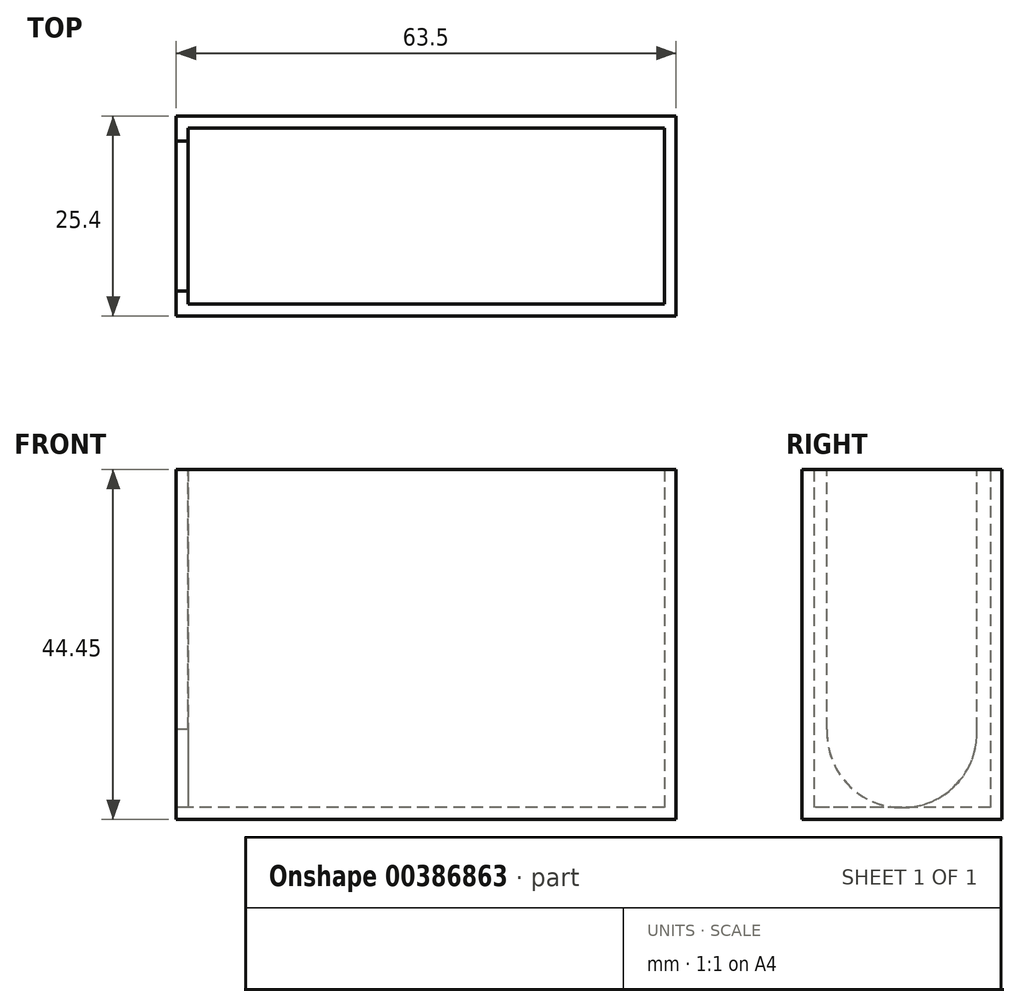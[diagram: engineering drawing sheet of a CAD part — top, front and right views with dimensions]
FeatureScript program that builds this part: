
annotation { "Feature Type Name" : "Feature", "Feature Type Description" : "" }
export const myFeature = defineFeature(function(context is Context, id is Id, definition is map)
    precondition{}
    {
        {
            var Q0;
            Q0=qCreatedBy(makeId("Top.planeOp"),FACE);
            var sketch = newSketch(context, id + "F0", { "sketchPlane" : qUnion([Q0])});
            skLineSegment(sketch, "E0.bottom", {"start": v(31.75, 12.7) * mm, "end": v(-31.75, 12.7) * mm});
            skLineSegment(sketch, "E0.top", {"start": v(31.75, -12.7) * mm, "end": v(-31.75, -12.7) * mm});
            skLineSegment(sketch, "E0.left", {"start": v(31.75, 12.7) * mm, "end": v(31.75, -12.7) * mm});
            skLineSegment(sketch, "E0.right", {"start": v(-31.75, 12.7) * mm, "end": v(-31.75, -12.7) * mm});
            skPoint(sketch, "E0.middle", {"position": v(0, 0) * mm});
            skSolve(sketch);
        }
        {
            var Q0;
            Q0=makeQuery(id+"F0.imprint","IMPRINT",FACE,{"disambiguationData":[TD([[makeQuery(id+"F0.imprint","IMPRINT",EDGE,{"derivedFrom":sQuery(id+"F0.wireOp",EDGE,"E0.bottom")}),1.0]])]});
            extrude(context, id + "F1", {"entities" : qUnion([Q0]), "depth" : 44.45 * mm});
        }
        {
            var Q0;
            Q0=makeQuery(id+"F1.opExtrude","CAP_FACE",FACE,{"disambiguationData":[OSD([sQuery(id+"F0.wireOp",EDGE,"E0.bottom"),sQuery(id+"F0.wireOp",EDGE,"E0.top"),sQuery(id+"F0.wireOp",EDGE,"E0.left"),sQuery(id+"F0.wireOp",EDGE,"E0.right")])],"isStart":false});
            shell(context, id + "F2", {"entities" : qUnion([Q0]), "thickness" : 1.5 * mm});
        }
        {
            var Q0;
            Q0=makeQuery(id+"F1.opExtrude","SWEPT_FACE",FACE,{"disambiguationData":[OSD([sQuery(id+"F0.wireOp",EDGE,"E0.right")])]});
            var sketch = newSketch(context, id + "F3", { "sketchPlane" : qUnion([Q0])});
            skCircle(sketch, "E1", {"center": v(0, 11.03) * mm, "radius": 9.53 * mm});
            skLineSegment(sketch, "E2.bottom", {"start": v(9.52, 11.43) * mm, "end": v(-9.53, 11.43) * mm});
            skLineSegment(sketch, "E2.top", {"start": v(9.52, 44.45) * mm, "end": v(-9.53, 44.45) * mm});
            skLineSegment(sketch, "E2.left", {"start": v(9.52, 11.43) * mm, "end": v(9.52, 44.45) * mm});
            skLineSegment(sketch, "E2.right", {"start": v(-9.53, 11.43) * mm, "end": v(-9.53, 44.45) * mm});
            skSolve(sketch);
        }
        {
            var Q0;
            {var subQ0=sQuery(id+"F3.wireOp",EDGE,"E2.bottom");var subQ1=sQuery(id+"F3.wireOp",EDGE,"E1");var subQ3=makeQuery(id+"F3.imprint","INTERSECT",VERTEX,{"derivedFrom":[subQ1,subQ0]});Q0=makeQuery(id+"F3.imprint","IMPRINT",FACE,{"disambiguationData":[TD([[makeQuery(id+"F3.imprint","IMPRINT",EDGE,{"disambiguationData":[TD([[subQ3,-1.0]])],"derivedFrom":subQ1}),1.0]])]});}
            var Q1;
            {var subQ0=sQuery(id+"F3.wireOp",EDGE,"E2.bottom");var subQ1=sQuery(id+"F3.wireOp",EDGE,"E1");var subQ2=makeQuery(id+"F3.imprint","INTERSECT",VERTEX,{"derivedFrom":[subQ1,subQ0]});Q1=makeQuery(id+"F3.imprint","IMPRINT",FACE,{"disambiguationData":[TD([[makeQuery(id+"F3.imprint","IMPRINT",EDGE,{"disambiguationData":[TD([[subQ2,1.0]])],"derivedFrom":subQ1}),1.0]])]});}
            var Q2;
            {var subQ1=sQuery(id+"F3.wireOp",EDGE,"E2.top");Q2=makeQuery(id+"F3.imprint","IMPRINT",FACE,{"disambiguationData":[TD([[makeQuery(id+"F3.imprint","IMPRINT",EDGE,{"derivedFrom":subQ1}),-1.0]])]});}
            extrude(context, id + "F4", {"entities" : qUnion([Q0, Q1, Q2]), "operationType" : NewBodyOperationType.REMOVE, "oppositeDirection" : true, "depth" : 1.5 * mm});
        }
    });
